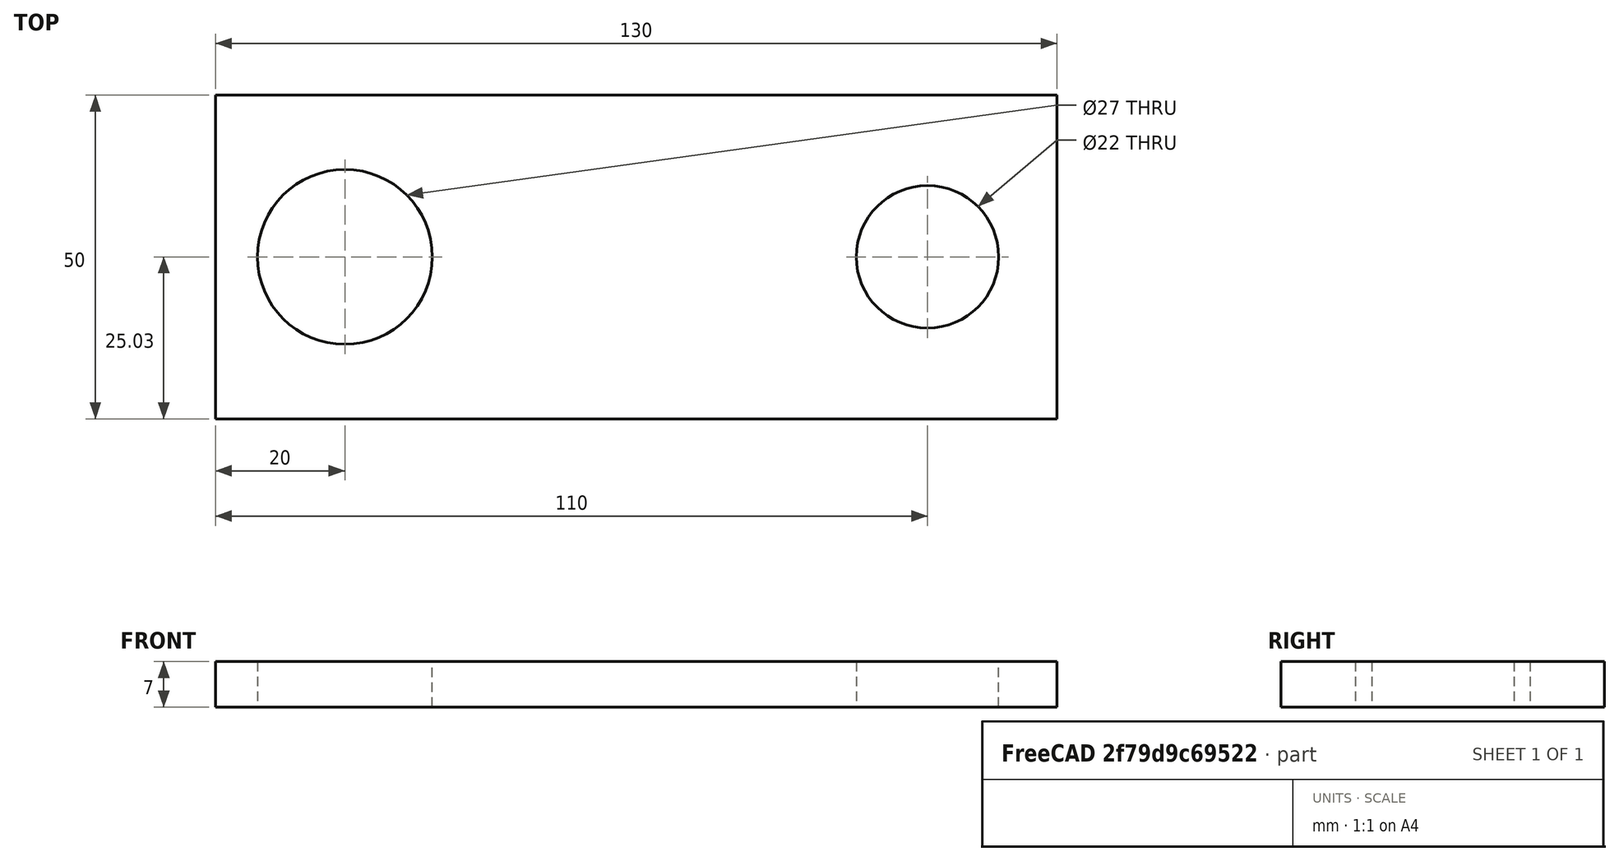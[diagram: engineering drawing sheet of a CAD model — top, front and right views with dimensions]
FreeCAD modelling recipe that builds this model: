
FCSTD DOCUMENT  (FreeCAD 0.19R24276 (Git))
Label: richag_3_130x5
License: All rights reserved
LicenseURL: http://en.wikipedia.org/wiki/All_rights_reserved
objects: Sketcher::SketchObject×1, PartDesign::Pad×1, PartDesign::Body×1
note: 4 computed .brp shape members not serialized (recipe doc carries the construction recipe); baked Part::Feature solids carry a one-line shape summary decoded from their .brp

FEATURE [Sketcher::SketchObject] Sketch
  FullyConstrained = false
  MapMode = 5
  Support = -> [XY_Plane]
  sketch-geometry (6):
    g0: Circle CenterX=0 CenterY=0 CenterZ=0 NormalX=0 NormalY=0 NormalZ=1 AngleXU=0 Radius=13.5
    g1: LineSegment StartX=-20 StartY=24.9744 StartZ=0 EndX=110 EndY=24.9744 EndZ=0
    g2: LineSegment StartX=-20 StartY=-25.0256 StartZ=0 EndX=-20 EndY=24.9744 EndZ=0
    g3: Circle CenterX=90 CenterY=0 CenterZ=0 NormalX=0 NormalY=0 NormalZ=1 AngleXU=0 Radius=11
    g4: LineSegment StartX=110 StartY=24.9744 StartZ=0 EndX=110 EndY=-25.0256 EndZ=0
    g5: LineSegment StartX=-20 StartY=-25.0256 StartZ=0 EndX=110 EndY=-25.0256 EndZ=0
  constraints (15):
    c: Diameter(g0) = 27
    c: Coincident(g2,g1)
    c: Horizontal(g1)
    c: Vertical(g2)
    c: Distance(g2) = 50
    c: DistanceX(g1,g0) = 20
    c: DistanceX(g1,g1) = 130
    c: Diameter(g3) = 22
    c: Coincident(g0,g-1)
    c: Coincident(g4,g1)
    c: Vertical(g4)
    c: Coincident(g5,g2)
    c: Coincident(g5,g4)
    c: Horizontal(g5)
    c: DistanceX(g0,g3) = 90
FEATURE [PartDesign::Pad] Pad
  Direction = (1,1,1)
  Length = 7
  Length2 = 100
  Profile = -> Sketch
  Type = 0
FEATURE [PartDesign::Body] Body
  Group = -> [Sketch,Pad]
  Origin = -> Origin
  Tip = -> Pad
